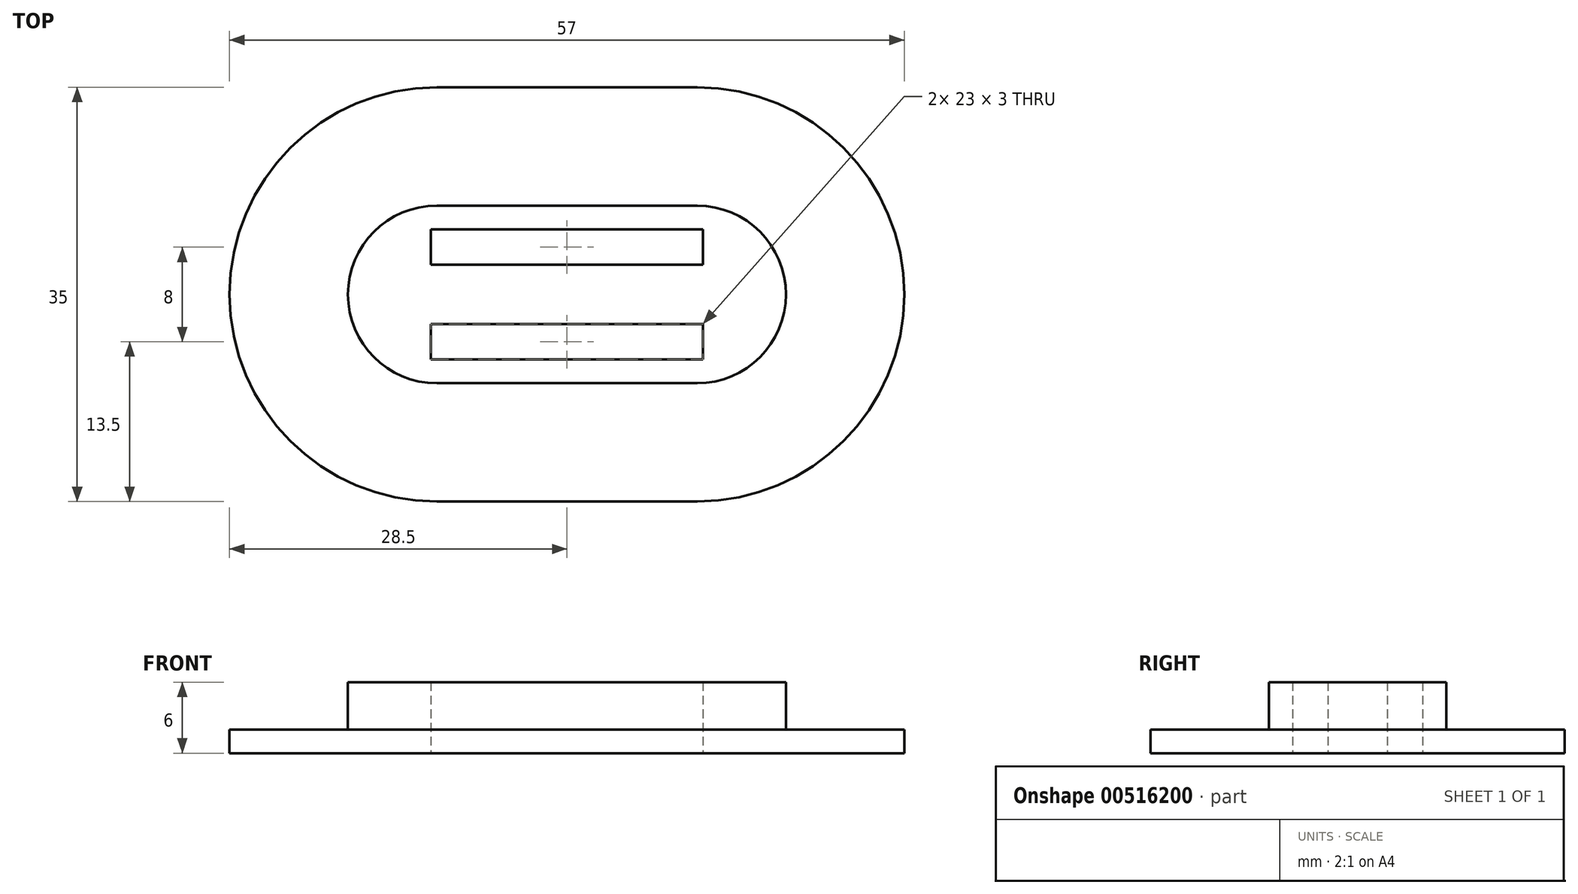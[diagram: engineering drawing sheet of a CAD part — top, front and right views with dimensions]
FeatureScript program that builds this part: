
annotation { "Feature Type Name" : "Feature", "Feature Type Description" : "" }
export const myFeature = defineFeature(function(context is Context, id is Id, definition is map)
    precondition{}
    {
        {
            var Q0;
            Q0=qCreatedBy(makeId("Top.planeOp"),FACE);
            var sketch = newSketch(context, id + "F0", { "sketchPlane" : qUnion([Q0])});
            skLineSegment(sketch, "E0.bottom", {"start": v(11, -7.5) * mm, "end": v(-11, -7.5) * mm});
            skLineSegment(sketch, "E0.top", {"start": v(11, 7.5) * mm, "end": v(-11, 7.5) * mm});
            skPoint(sketch, "E0.middle", {"position": v(0, 0) * mm});
            skArc(sketch, "E1", {"start": v(-11, 7.5) * mm, "mid": v(-18.5, 0) * mm, "end": v(-11, -7.5) * mm});
            skArc(sketch, "E2", {"start": v(11, -7.5) * mm, "mid": v(18.5, 0) * mm, "end": v(11, 7.5) * mm});
            skLineSegment(sketch, "E3.bottom", {"start": v(11.5, 2.5) * mm, "end": v(-11.5, 2.5) * mm});
            skLineSegment(sketch, "E3.top", {"start": v(11.5, 5.5) * mm, "end": v(-11.5, 5.5) * mm});
            skLineSegment(sketch, "E3.left", {"start": v(11.5, 2.5) * mm, "end": v(11.5, 5.5) * mm});
            skLineSegment(sketch, "E3.right", {"start": v(-11.5, 2.5) * mm, "end": v(-11.5, 5.5) * mm});
            skPoint(sketch, "E3.middle", {"position": v(0, 4) * mm});
            skLineSegment(sketch, "E4.MirrorCS", {"start": v(11.5, -2.5) * mm, "end": v(-11.5, -2.5) * mm});
            skLineSegment(sketch, "E5.MirrorCS", {"start": v(-11.5, -2.5) * mm, "end": v(-11.5, -5.5) * mm});
            skLineSegment(sketch, "E6.MirrorCS", {"start": v(11.5, -5.5) * mm, "end": v(-11.5, -5.5) * mm});
            skLineSegment(sketch, "E7.MirrorCS", {"start": v(11.5, -2.5) * mm, "end": v(11.5, -5.5) * mm});
            skArc(sketch, "E8.0", {"start": v(-11, 17.5) * mm, "mid": v(-28.5, 0) * mm, "end": v(-11, -17.5) * mm});
            skLineSegment(sketch, "E8.1", {"start": v(11, 17.5) * mm, "end": v(-11, 17.5) * mm});
            skArc(sketch, "E8.2", {"start": v(11, -17.5) * mm, "mid": v(28.5, 0) * mm, "end": v(11, 17.5) * mm});
            skLineSegment(sketch, "E8.3", {"start": v(11, -17.5) * mm, "end": v(-11, -17.5) * mm});
            skSolve(sketch);
        }
        {
            var Q0;
            Q0=makeQuery(id+"F0.imprint","IMPRINT",FACE,{"disambiguationData":[TD([[makeQuery(id+"F0.imprint","IMPRINT",EDGE,{"derivedFrom":sQuery(id+"F0.wireOp",EDGE,"E0.bottom")}),-1.0]])]});
            var Q1;
            Q1=makeQuery(id+"F0.imprint","IMPRINT",FACE,{"disambiguationData":[TD([[makeQuery(id+"F0.imprint","IMPRINT",EDGE,{"derivedFrom":sQuery(id+"F0.wireOp",EDGE,"E0.bottom")}),1.0]])]});
            extrude(context, id + "F1", {"entities" : qUnion([Q0, Q1]), "depth" : 2 * mm, "offsetDistance" : 25 * mm});
        }
        {
            var Q0;
            Q0=makeQuery(id+"F0.imprint","IMPRINT",FACE,{"disambiguationData":[TD([[makeQuery(id+"F0.imprint","IMPRINT",EDGE,{"derivedFrom":sQuery(id+"F0.wireOp",EDGE,"E0.bottom")}),-1.0]])]});
            extrude(context, id + "F2", {"entities" : qUnion([Q0]), "operationType" : NewBodyOperationType.ADD, "depth" : 6 * mm, "offsetDistance" : 25 * mm});
        }
    });
